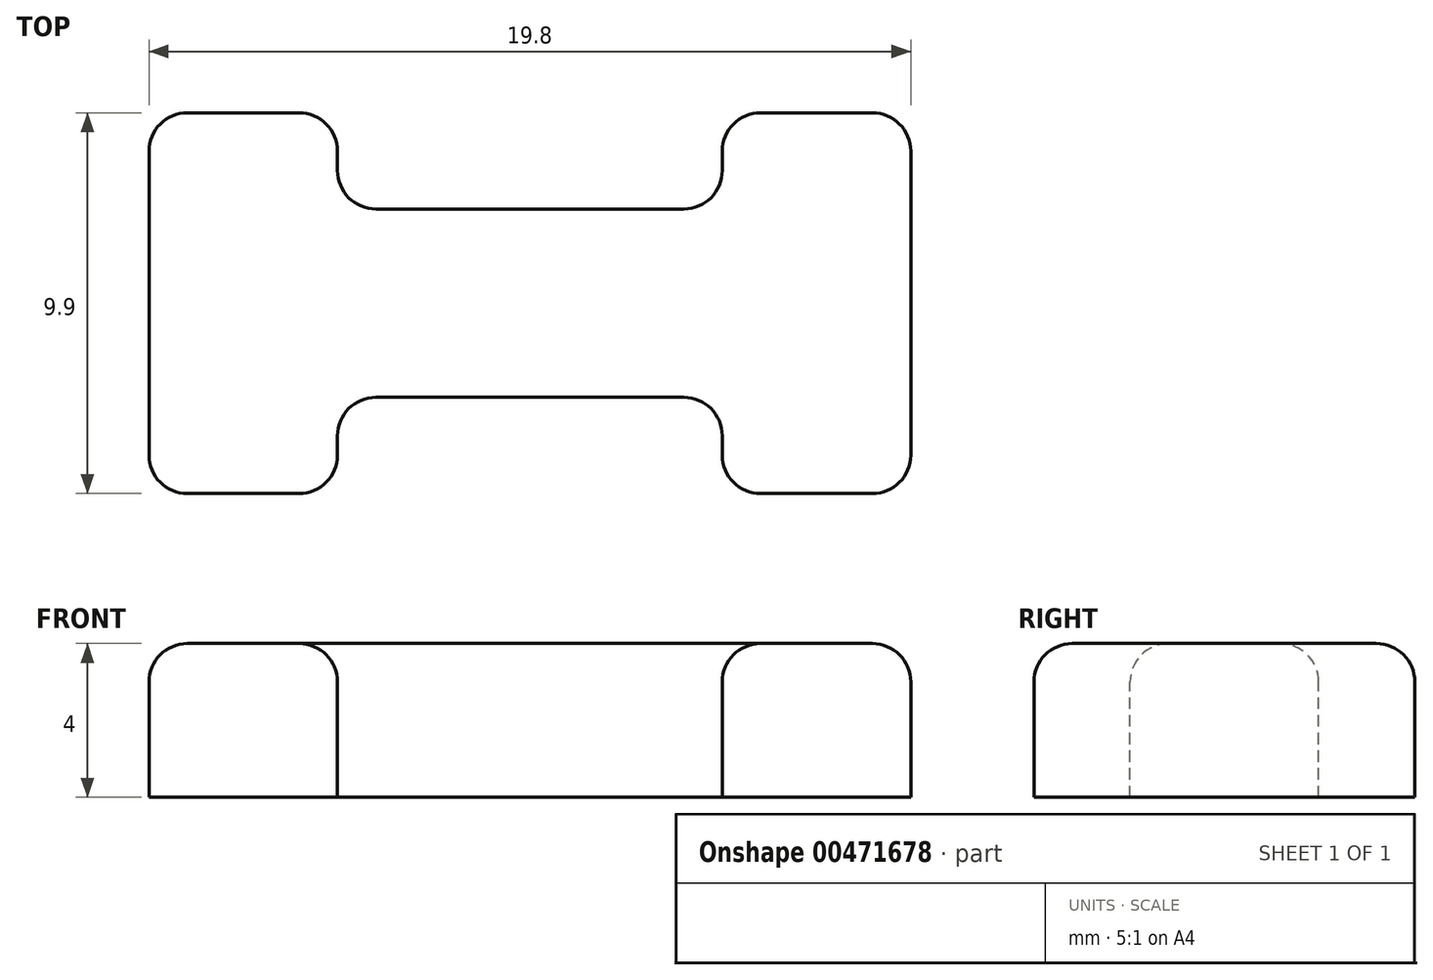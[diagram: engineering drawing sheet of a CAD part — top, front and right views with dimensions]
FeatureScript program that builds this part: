
annotation { "Feature Type Name" : "Feature", "Feature Type Description" : "" }
export const myFeature = defineFeature(function(context is Context, id is Id, definition is map)
    precondition{}
    {
        {
            var Q0;
            Q0=qCreatedBy(makeId("Top.planeOp"),FACE);
            var sketch = newSketch(context, id + "F0", { "sketchPlane" : qUnion([Q0])});
            skLineSegment(sketch, "E0.bottom", {"start": v(5, -2.45) * mm, "end": v(-5, -2.45) * mm});
            skLineSegment(sketch, "E0.top", {"start": v(5, 2.45) * mm, "end": v(-5, 2.45) * mm});
            skLineSegment(sketch, "E0.left", {"start": v(5, -2.45) * mm, "end": v(5, 2.45) * mm});
            skLineSegment(sketch, "E0.right", {"start": v(-5, -2.45) * mm, "end": v(-5, 2.45) * mm});
            skPoint(sketch, "E0.middle", {"position": v(0, 0) * mm});
            skLineSegment(sketch, "E1", {"start": v(-5, 0) * mm, "end": v(11.95, 0) * mm, "construction": true});
            skLineSegment(sketch, "E2", {"start": v(-5, 0) * mm, "end": v(-16.4, 0) * mm, "construction": true});
            skLineSegment(sketch, "E3", {"start": v(-5, 2.45) * mm, "end": v(-5, 4.95) * mm});
            skLineSegment(sketch, "E4", {"start": v(-5, 4.95) * mm, "end": v(-9.9, 4.95) * mm});
            skLineSegment(sketch, "E5", {"start": v(-9.9, 4.95) * mm, "end": v(-9.9, -4.95) * mm});
            skLineSegment(sketch, "E6", {"start": v(-9.9, -4.95) * mm, "end": v(-5, -4.95) * mm});
            skLineSegment(sketch, "E7", {"start": v(-5, -4.95) * mm, "end": v(-5, -2.45) * mm});
            skLineSegment(sketch, "E8", {"start": v(5, 2.45) * mm, "end": v(5, 4.95) * mm});
            skLineSegment(sketch, "E9", {"start": v(5, 4.95) * mm, "end": v(9.9, 4.95) * mm});
            skLineSegment(sketch, "E10", {"start": v(9.9, 4.95) * mm, "end": v(9.9, -4.95) * mm});
            skLineSegment(sketch, "E11", {"start": v(9.9, -4.95) * mm, "end": v(5, -4.95) * mm});
            skLineSegment(sketch, "E12", {"start": v(5, -4.95) * mm, "end": v(5, -2.45) * mm});
            skSolve(sketch);
        }
        {
            var Q0;
            Q0=makeQuery(id+"F0.imprint","IMPRINT",FACE,{"disambiguationData":[TD([[makeQuery(id+"F0.imprint","IMPRINT",EDGE,{"derivedFrom":sQuery(id+"F0.wireOp",EDGE,"E0.right")}),1.0]])]});
            var Q1;
            Q1=makeQuery(id+"F0.imprint","IMPRINT",FACE,{"disambiguationData":[TD([[makeQuery(id+"F0.imprint","IMPRINT",EDGE,{"derivedFrom":sQuery(id+"F0.wireOp",EDGE,"E0.left")}),-1.0]])]});
            var Q2;
            Q2=makeQuery(id+"F0.imprint","IMPRINT",FACE,{"disambiguationData":[TD([[makeQuery(id+"F0.imprint","IMPRINT",EDGE,{"derivedFrom":sQuery(id+"F0.wireOp",EDGE,"E0.bottom")}),-1.0]])]});
            extrude(context, id + "F1", {"entities" : qUnion([Q0, Q1, Q2]), "oppositeDirection" : true, "depth" : 4 * mm});
        }
        {
            var Q0;
            Q0=makeQuery(id+"F1.opExtrude","SWEPT_EDGE",EDGE,{"disambiguationData":[OSD([sQuery(id+"F0.wireOp",EDGE,"E0.top"),sQuery(id+"F0.wireOp",EDGE,"E0.right"),sQuery(id+"F0.wireOp",EDGE,"E3")])]});
            var Q1;
            Q1=makeQuery(id+"F1.opExtrude","SWEPT_EDGE",EDGE,{"disambiguationData":[OSD([sQuery(id+"F0.wireOp",EDGE,"E3"),sQuery(id+"F0.wireOp",EDGE,"E4")])]});
            var Q2;
            Q2=makeQuery(id+"F1.opExtrude","SWEPT_EDGE",EDGE,{"disambiguationData":[OSD([sQuery(id+"F0.wireOp",EDGE,"E4"),sQuery(id+"F0.wireOp",EDGE,"E5")])]});
            var Q3;
            Q3=makeQuery(id+"F1.opExtrude","SWEPT_EDGE",EDGE,{"disambiguationData":[OSD([sQuery(id+"F0.wireOp",EDGE,"E5"),sQuery(id+"F0.wireOp",EDGE,"E6")])]});
            var Q4;
            Q4=makeQuery(id+"F1.opExtrude","SWEPT_EDGE",EDGE,{"disambiguationData":[OSD([sQuery(id+"F0.wireOp",EDGE,"E11"),sQuery(id+"F0.wireOp",EDGE,"E12")])]});
            var Q5;
            Q5=makeQuery(id+"F1.opExtrude","SWEPT_EDGE",EDGE,{"disambiguationData":[OSD([sQuery(id+"F0.wireOp",EDGE,"E6"),sQuery(id+"F0.wireOp",EDGE,"E7")])]});
            var Q6;
            Q6=makeQuery(id+"F1.opExtrude","SWEPT_EDGE",EDGE,{"disambiguationData":[OSD([sQuery(id+"F0.wireOp",EDGE,"E0.bottom"),sQuery(id+"F0.wireOp",EDGE,"E0.right"),sQuery(id+"F0.wireOp",EDGE,"E7")])]});
            var Q7;
            Q7=makeQuery(id+"F1.opExtrude","SWEPT_EDGE",EDGE,{"disambiguationData":[OSD([sQuery(id+"F0.wireOp",EDGE,"E8"),sQuery(id+"F0.wireOp",EDGE,"E9")])]});
            var Q8;
            Q8=makeQuery(id+"F1.opExtrude","SWEPT_EDGE",EDGE,{"disambiguationData":[OSD([sQuery(id+"F0.wireOp",EDGE,"E0.bottom"),sQuery(id+"F0.wireOp",EDGE,"E0.left"),sQuery(id+"F0.wireOp",EDGE,"E12")])]});
            var Q9;
            Q9=makeQuery(id+"F1.opExtrude","SWEPT_EDGE",EDGE,{"disambiguationData":[OSD([sQuery(id+"F0.wireOp",EDGE,"E9"),sQuery(id+"F0.wireOp",EDGE,"E10")])]});
            var Q10;
            Q10=makeQuery(id+"F1.opExtrude","SWEPT_EDGE",EDGE,{"disambiguationData":[OSD([sQuery(id+"F0.wireOp",EDGE,"E10"),sQuery(id+"F0.wireOp",EDGE,"E11")])]});
            var Q11;
            Q11=makeQuery(id+"F1.opExtrude","SWEPT_EDGE",EDGE,{"disambiguationData":[OSD([sQuery(id+"F0.wireOp",EDGE,"E0.top"),sQuery(id+"F0.wireOp",EDGE,"E0.left"),sQuery(id+"F0.wireOp",EDGE,"E8")])]});
            var Q12;
            Q12=makeQuery(id+"F1.opExtrude","CAP_FACE",FACE,{"disambiguationData":[OSD([sQuery(id+"F0.wireOp",EDGE,"E0.bottom"),sQuery(id+"F0.wireOp",EDGE,"E0.top"),sQuery(id+"F0.wireOp",EDGE,"E3"),sQuery(id+"F0.wireOp",EDGE,"E4"),sQuery(id+"F0.wireOp",EDGE,"E5"),sQuery(id+"F0.wireOp",EDGE,"E6"),sQuery(id+"F0.wireOp",EDGE,"E7"),sQuery(id+"F0.wireOp",EDGE,"E8"),sQuery(id+"F0.wireOp",EDGE,"E9"),sQuery(id+"F0.wireOp",EDGE,"E10"),sQuery(id+"F0.wireOp",EDGE,"E11"),sQuery(id+"F0.wireOp",EDGE,"E12")])],"isStart":true});
            fillet(context, id + "F2", {"entities" : qUnion([Q0, Q1, Q2, Q3, Q4, Q5, Q6, Q7, Q8, Q9, Q10, Q11, Q12]), "radius" : 1 * mm, "tangentPropagation" : true, "allowEdgeOverflow" : false});
        }
    });
